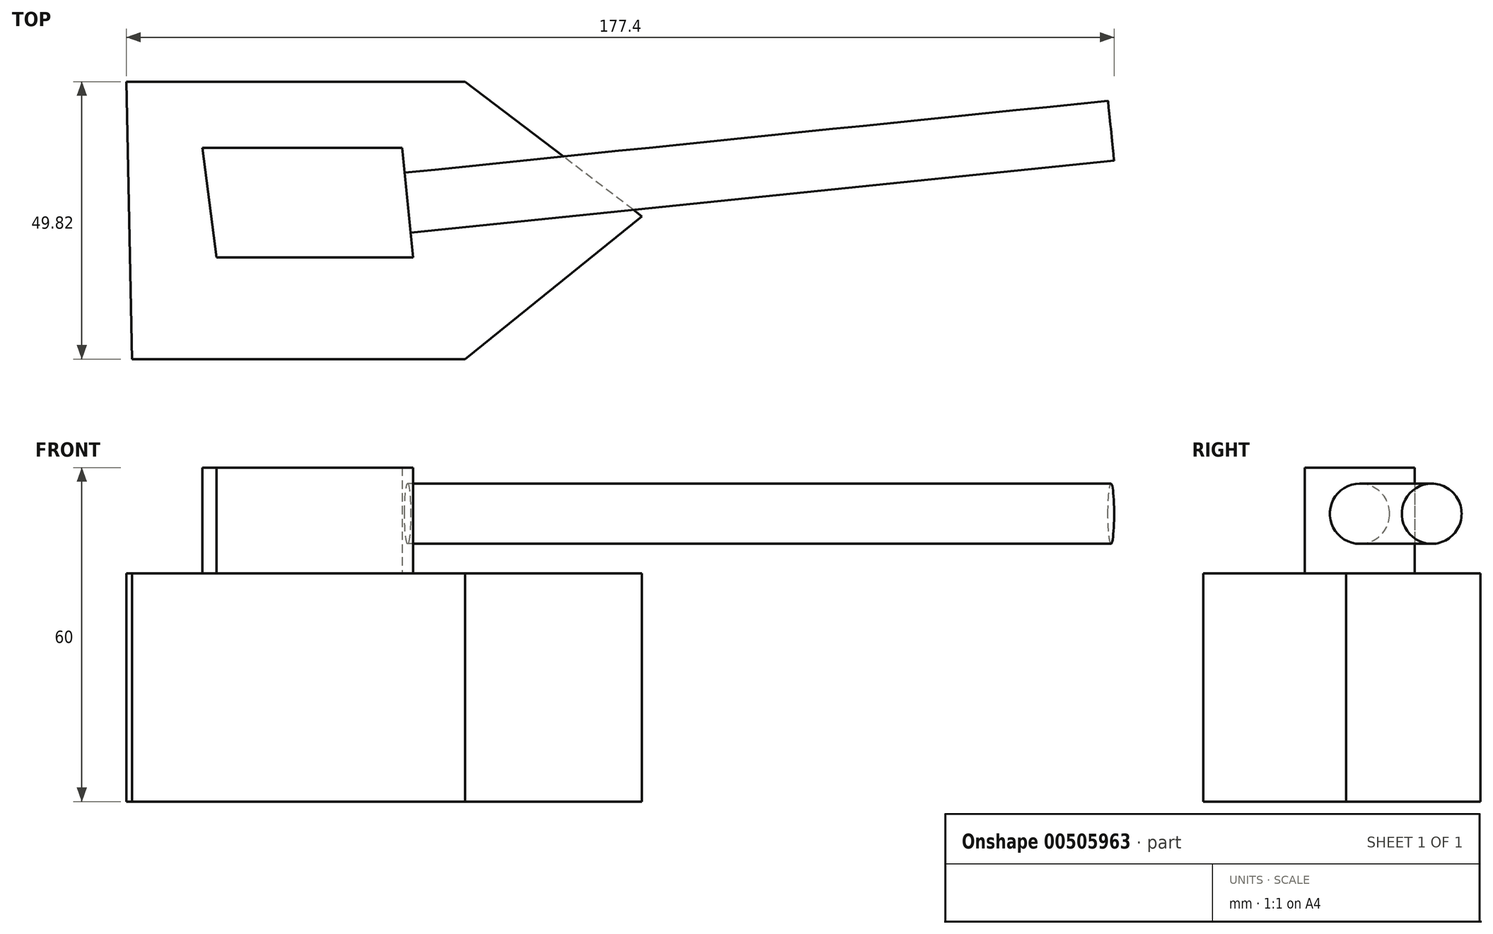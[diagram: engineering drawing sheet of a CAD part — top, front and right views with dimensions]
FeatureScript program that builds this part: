
annotation { "Feature Type Name" : "Feature", "Feature Type Description" : "" }
export const myFeature = defineFeature(function(context is Context, id is Id, definition is map)
    precondition{}
    {
        {
            var Q0;
            Q0=qCreatedBy(makeId("Top.planeOp"),FACE);
            var sketch = newSketch(context, id + "F0", { "sketchPlane" : qUnion([Q0])});
            skLineSegment(sketch, "E0", {"start": v(-41.68, -18.24) * mm, "end": v(18.13, -18.24) * mm});
            skLineSegment(sketch, "E1", {"start": v(18.13, -18.24) * mm, "end": v(49.87, 7.42) * mm});
            skLineSegment(sketch, "E2", {"start": v(49.87, 7.42) * mm, "end": v(18.13, 31.58) * mm});
            skLineSegment(sketch, "E3", {"start": v(18.13, 31.58) * mm, "end": v(-42.68, 31.58) * mm});
            skLineSegment(sketch, "E4", {"start": v(-42.68, 31.58) * mm, "end": v(-41.68, -18.24) * mm});
            skSolve(sketch);
        }
        {
            var Q0;
            Q0=makeQuery(id+"F0.imprint","IMPRINT",FACE,{"disambiguationData":[TD([[makeQuery(id+"F0.imprint","IMPRINT",EDGE,{"derivedFrom":sQuery(id+"F0.wireOp",EDGE,"E0")}),1.0]])]});
            extrude(context, id + "F1", {"entities" : qUnion([Q0]), "depth" : 41 * mm});
        }
        {
            var Q0;
            Q0=makeQuery(id+"F1.opExtrude","CAP_FACE",FACE,{"disambiguationData":[OSD([sQuery(id+"F0.wireOp",EDGE,"E0"),sQuery(id+"F0.wireOp",EDGE,"E1"),sQuery(id+"F0.wireOp",EDGE,"E2"),sQuery(id+"F0.wireOp",EDGE,"E3"),sQuery(id+"F0.wireOp",EDGE,"E4")])],"isStart":false});
            var sketch = newSketch(context, id + "F2", { "sketchPlane" : qUnion([Q0])});
            skLineSegment(sketch, "E5", {"start": v(-29.04, 19.73) * mm, "end": v(6.82, 19.73) * mm});
            skLineSegment(sketch, "E6", {"start": v(6.82, 19.73) * mm, "end": v(8.84, 0) * mm});
            skLineSegment(sketch, "E7", {"start": v(8.84, 0) * mm, "end": v(-26.49, 0) * mm});
            skLineSegment(sketch, "E8", {"start": v(-26.49, 0) * mm, "end": v(-29.04, 19.73) * mm});
            skSolve(sketch);
        }
        {
            var Q0;
            Q0=makeQuery(id+"F2.imprint","IMPRINT",FACE,{"disambiguationData":[TD([[makeQuery(id+"F2.imprint","IMPRINT",EDGE,{"derivedFrom":sQuery(id+"F2.wireOp",EDGE,"E5")}),-1.0]])]});
            extrude(context, id + "F3", {"entities" : qUnion([Q0]), "operationType" : NewBodyOperationType.ADD, "depth" : 19 * mm});
        }
        {
            var Q0;
            Q0=makeQuery(id+"F3.opExtrude","SWEPT_FACE",FACE,{"disambiguationData":[OSD([sQuery(id+"F2.wireOp",EDGE,"E6")])]});
            var sketch = newSketch(context, id + "F4", { "sketchPlane" : qUnion([Q0])});
            skCircle(sketch, "E9", {"center": v(9.02, 51.7) * mm, "radius": 5.4 * mm});
            skPoint(sketch, "E9.centerSnap0", {"position": v(9.02, 41) * mm});
            skSolve(sketch);
        }
        {
            var Q0;
            Q0=makeQuery(id+"F4.imprint","IMPRINT",FACE,{"disambiguationData":[TD([[makeQuery(id+"F4.imprint","IMPRINT",EDGE,{"derivedFrom":sQuery(id+"F4.wireOp",EDGE,"E9")}),1.0]])]});
            extrude(context, id + "F5", {"entities" : qUnion([Q0]), "operationType" : NewBodyOperationType.ADD, "depth" : 127 * mm});
        }
    });
